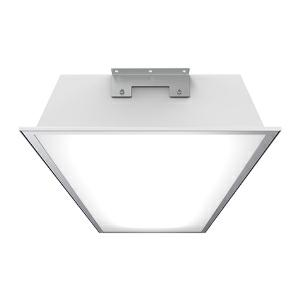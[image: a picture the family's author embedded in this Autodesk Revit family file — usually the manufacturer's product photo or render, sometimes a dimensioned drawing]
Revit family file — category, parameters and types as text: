
# Revit family: 3f_filippi_-_beta_500_va_3f_filippi_-_52072_-_beta_500_150w-840_va_l870
name_source: partatom
category: Lighting Fixtures
units: mm (PartAtom-declared; Revit-internal decimal feet)

## family parameters
Cut with Voids When Loaded = No
Host = Face
Light Source = No
Part Type = Normal
Room Calculation Point = No
Round Connector Dimension = Use Diameter
Shared = No

## types (1)
- 3F Filippi - Beta 500 VA (1 x LED, 25990 lm, 162 W, 4000 K)
    Apparent Load = 162 VA
    Approval mark = CE
    CIE Flux Codes = 51 82 97 100 100
    Color Rendering = 80
    Color Temperature = 4000 K
    Control Gear = Electronic ballast
    Default Elevation = 1800 mm
    Description = ILLUMINOTECHNICAL
Luminous efficiency 100% (DLOR 100%, ULOR 0%).
Initial luminous flux of the luminaire 25990 lm.
Direct symmetric medium distribution.
Installation Interdistance Transv.D = 1.24 x hu - Long.D = 1.23 x hu.
Tabular UGR (CIE 117 - 4H-8H; S=0.25H; 70/50/20): RUG 26.1 - 26.3.
Beam angle: 104° - 104°.
Luminous efficacy 160 lm/W.
Lifetime (L93/B10): 30000 h. (tq+25°C)
Lifetime (L90/B10): 50000 h. (tq+25°C)
Lifetime (L85/B10): 80000 h. (tq+25°C)
Lifetime (L80/B10): 100000 h. (tq+25°C)
Lifetime (L85/B10): 50000 h. (tq+50°C)
Sudden decreased luminous flux after 50000 hours: 0% (C0).
Photobiological safety in compliance with IEC/TR 62778: RG0 risk exempt, (IEC 62471).
In compliance with IEC/EN 62722-2-1 - IEC/EN 62717 standards.

SOURCE
3 linear LED modules 52W/840.
Energy efficiency class (UE 2019/2020 - UE 2019/2015): C.
CIE 13.3 Colour rendering index: CRI >80 (R9 <50%).
IES TM-30 Fidelity Index: Rf = 84 Rg = 95.
CCT nominal colour temperature 4000 K.
Colour initial tolerance (MacAdam): SDCM 3.

MECHANICAL
Housing in white painted epoxy-polyester powder aluminium.
White aluminium non-iridescent high efficiency.
Frosted glass HST tempered, non-combustible.
Perimetrical frame in stainless steel with vandal-proof opening and stainless steel nuts and bolts.
Polyurethane foam seal, ecological, anti-aging, installed using a continuous automatic process with no joints.
Fixing bracket in stainless steel.
Luminaire with limited surface temperature. - D - (EN 60598-2-24)
Dimensions: 870x515 mm, height 105 mm. Weight 11.11 kg.
IP66 protection degree.
Mechanical strength to impacts IK08 (5 joule).
Glow-wire test resistance 960°C.

ELECTRICAL
Halogen Free electronic wiring 230V-50/60Hz, power factor 0.95, THD <25%, constant output current, class I, 1 driver.
Power of the luminaire 162 W.
ENEC - CE.
SAFE FLICKER: PstLM=<1 and SVM=<0.4 (IEC TR 61547-1 and IEC TR 63158), to ensure a more comfortable and safe light.
Luminaire compliant with EN 60598-2-22 for power supply from a centralised emergency system CPSS (Central Power Supply System), not incorporated in the luminaire - high risk areas excluded. The default power and flux are 100% in AC and 100% in DC.
Ambient temperature from -20°C to +50°C.
Temperature class T6 max 85°C.
Quick connection via M20 3P connector with 9-13 mm tightening range.
Quick connection in polycarbonate with M20x1,5 cable gland, to access the terminal block positioned on a removable runner.
Relative humidity UR: <85%.

INSTALLATION
Ceiling / Suspended.
All accessories dedicated to this product are available on the Catalog and on our website www.3F-Filippi.com.

APPLICATIONS
Commercial and industrial environments and warehouses.

WARNING
Fixture not suitable for cold stores with an ambient temperature <0°C and/or relative humidity >85%.
Luminaire designed for disposal/recycling at end-of-life.
Replaceable (LED only) light source by a professional. Replaceable control gear by a professional.
    Height = 105 mm
    Lamp = 1 x LED
    Lamp Light Flux = 25990 lm
    Lamp Power = 162 W
    Lamp count = 1
    Length = 870 mm
    Lifetime = 50000 h
    Luminous efficacy = 160 lm/W
    Manufacturer = 3F Filippi
    ModVariant = No
    Model = 3F Filippi - 52072 - Beta 500 150W-840 VA L870
    Mounting Place = Ceiling
    Mounting Type = Pendant
    Number of Poles = 1
    OnlyDefault = Yes
    Power Factor = 1
    Product Name = 3F Filippi - Beta 500 VA
    Product group = pendant luminaire
    ProductGroupID = 9
    Protection Class = Protection class I
    Protection Degree = IP 66
    RLX_Detail_Level = 1
    RLX_Emergency_Light_Flux = 0 lm
    RLX_Emergency_Type = 0
    RLX_Emergency_Type_DB = No
    RlxData = <blob elided: 119229 chars, md5=d47ba059>
    Socket = socket
    Standby Power = 0 W
    System Light Flux = 25990 lm
    System Power = 162 W
    Type Comments = Product without accessories
    Type Image = 3ffilippi_beta_500_va.jpg
    URL = http://relux.com
    VarID = ---
    Voltage = 0 V
    Weight = 0.00 kg
    Width = 515 mm

## geometry (parser evidence)
native form markers: Blend x4, Sweep x9
no freeform markers — native parametric forms only
